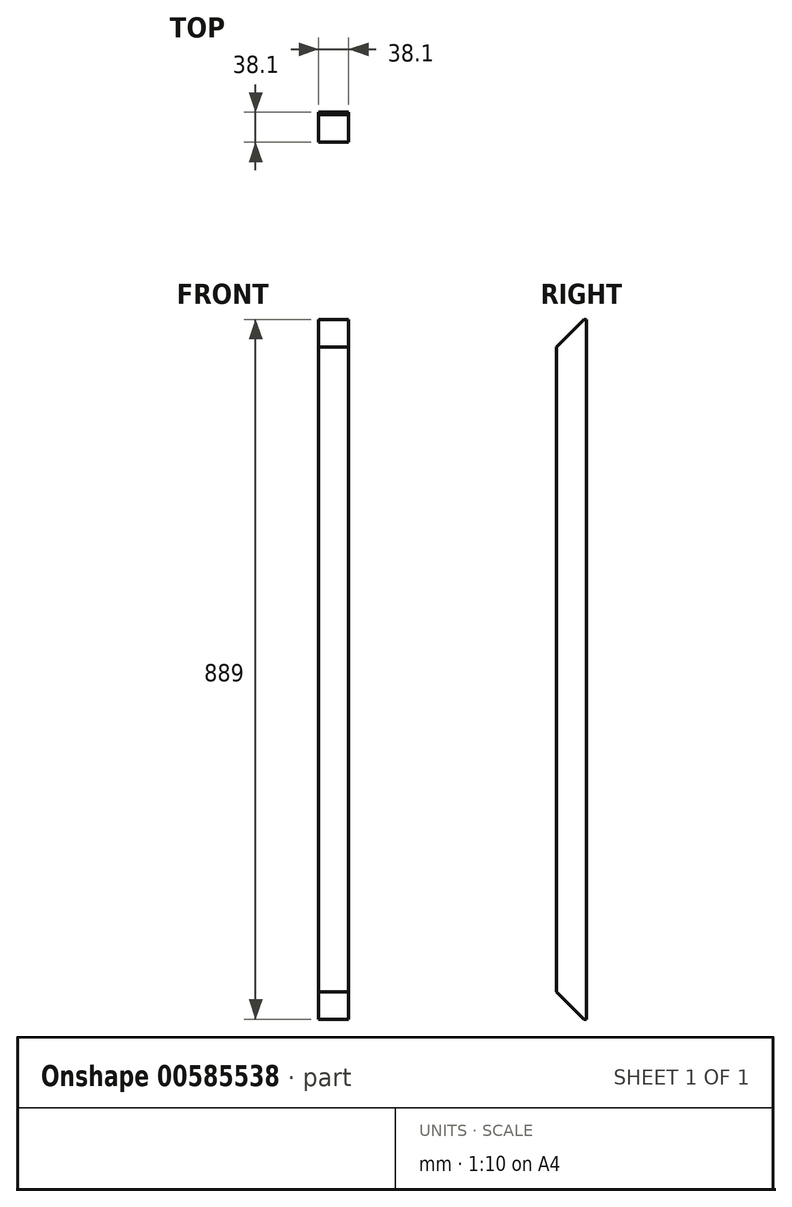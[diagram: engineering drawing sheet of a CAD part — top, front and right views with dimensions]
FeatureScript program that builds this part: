
annotation { "Feature Type Name" : "Feature", "Feature Type Description" : "" }
export const myFeature = defineFeature(function(context is Context, id is Id, definition is map)
    precondition{}
    {
        {
            var Q0;
            Q0=qCreatedBy(makeId("Front.planeOp"),FACE);
            var sketch = newSketch(context, id + "F0", { "sketchPlane" : qUnion([Q0])});
            skLineSegment(sketch, "E0.bottom", {"start": v(0, 0) * mm, "end": v(38.1, 0) * mm});
            skLineSegment(sketch, "E0.top", {"start": v(0, 889) * mm, "end": v(38.1, 889) * mm});
            skLineSegment(sketch, "E0.left", {"start": v(0, 0) * mm, "end": v(0, 889) * mm});
            skLineSegment(sketch, "E0.right", {"start": v(38.1, 0) * mm, "end": v(38.1, 889) * mm});
            skSolve(sketch);
        }
        {
            var Q0;
            Q0 = qSketchRegion(id + "F0", true);
            extrude(context, id + "F1", {"entities" : qUnion([Q0]), "depth" : 38.1 * mm, "offsetDistance" : 25.4 * mm});
        }
        {
            var Q0;
            Q0=makeQuery(id+"F1.opExtrude","SWEPT_FACE",FACE,{"disambiguationData":[OSD([sQuery(id+"F0.wireOp",EDGE,"E0.left")])]});
            var sketch = newSketch(context, id + "F2", { "sketchPlane" : qUnion([Q0])});
            skLineSegment(sketch, "E1", {"start": v(3.17, 889) * mm, "end": v(38.1, 854.08) * mm});
            skLineSegment(sketch, "E2", {"start": v(38.1, 854.08) * mm, "end": v(38.1, 889) * mm});
            skLineSegment(sketch, "E3", {"start": v(38.1, 889) * mm, "end": v(3.18, 889) * mm});
            skLineSegment(sketch, "E4", {"start": v(3.17, 0) * mm, "end": v(38.1, 34.93) * mm});
            skLineSegment(sketch, "E5", {"start": v(38.1, 34.93) * mm, "end": v(38.1, 0) * mm});
            skLineSegment(sketch, "E6", {"start": v(38.1, 0) * mm, "end": v(3.18, 0) * mm});
            skSolve(sketch);
        }
        {
            var Q0;
            Q0 = qSketchRegion(id + "F2", true);
            extrude(context, id + "F3", {"entities" : qUnion([Q0]), "operationType" : NewBodyOperationType.REMOVE, "endBound" : BoundingType.THROUGH_ALL, "oppositeDirection" : true, "depth" : 25.4 * mm, "offsetDistance" : 25.4 * mm});
        }
    });
